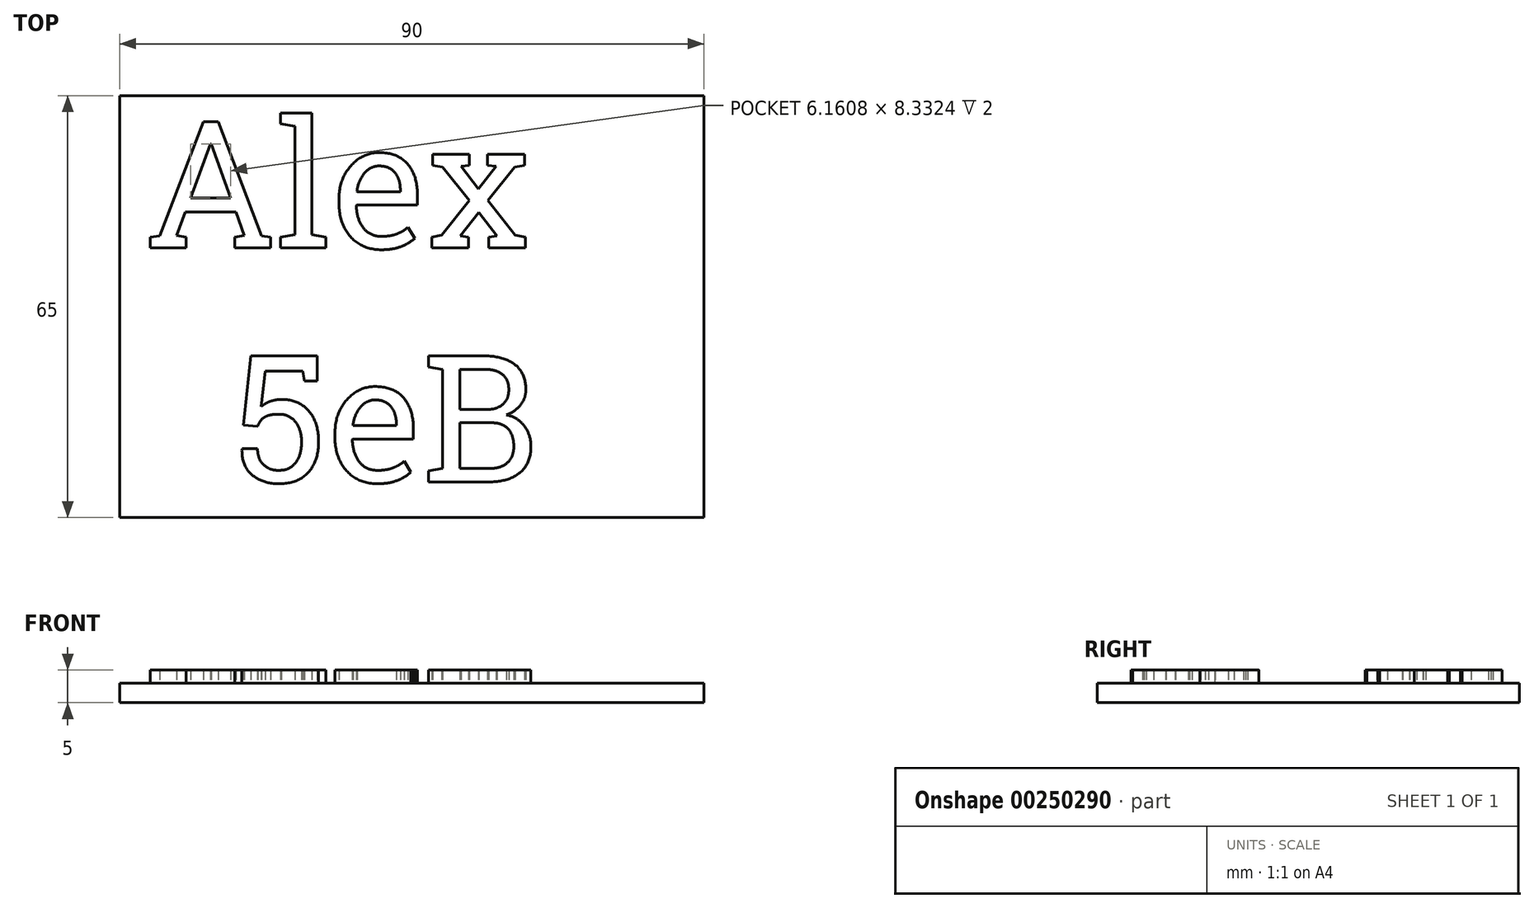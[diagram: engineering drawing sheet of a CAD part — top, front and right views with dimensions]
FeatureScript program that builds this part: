
annotation { "Feature Type Name" : "Feature", "Feature Type Description" : "" }
export const myFeature = defineFeature(function(context is Context, id is Id, definition is map)
    precondition{}
    {
        {
            var Q0;
            Q0=qCreatedBy(makeId("Top.planeOp"),FACE);
            var sketch = newSketch(context, id + "F0", { "sketchPlane" : qUnion([Q0])});
            skPoint(sketch, "E0.middle", {"position": v(0, 0) * mm});
            skLineSegment(sketch, "E1.bottom", {"start": v(0, 0) * mm, "end": v(90, 0) * mm});
            skLineSegment(sketch, "E1.top", {"start": v(0, -65) * mm, "end": v(90, -65) * mm});
            skLineSegment(sketch, "E1.left", {"start": v(0, 0) * mm, "end": v(0, -65) * mm});
            skLineSegment(sketch, "E1.right", {"start": v(90, 0) * mm, "end": v(90, -65) * mm});
            skSolve(sketch);
        }
        {
            var Q0;
            Q0=makeQuery(id+"F0.imprint","IMPRINT",FACE,{"disambiguationData":[TD([[makeQuery(id+"F0.imprint","IMPRINT",EDGE,{"derivedFrom":sQuery(id+"F0.wireOp",EDGE,"E1.bottom")}),-1.0]])]});
            extrude(context, id + "F1", {"entities" : qUnion([Q0]), "depth" : 3 * mm});
        }
        {
            var Q0;
            Q0=makeQuery(id+"F1.opExtrude","CAP_FACE",FACE,{"disambiguationData":[OSD([sQuery(id+"F0.wireOp",EDGE,"E1.bottom"),sQuery(id+"F0.wireOp",EDGE,"E1.top"),sQuery(id+"F0.wireOp",EDGE,"E1.left"),sQuery(id+"F0.wireOp",EDGE,"E1.right")])],"isStart":false});
            var sketch = newSketch(context, id + "F2", { "sketchPlane" : qUnion([Q0])});
            skText(sketch, "E2", { "text": "Alex\n  5eB", "fontName": "RobotoSlab-Regular.ttf"});
            const initialGuessF2  = {"E2": [0.00397, -0.02346, 1, 0, 0.01966]};
            skSetInitialGuess(sketch, initialGuessF2);
            skSolve(sketch);
        }
        {
            var Q0;
            Q0 = qSketchRegion(id + "F2", true);
            extrude(context, id + "F3", {"entities" : qUnion([Q0]), "operationType" : NewBodyOperationType.ADD, "depth" : 2 * mm});
        }
    });
